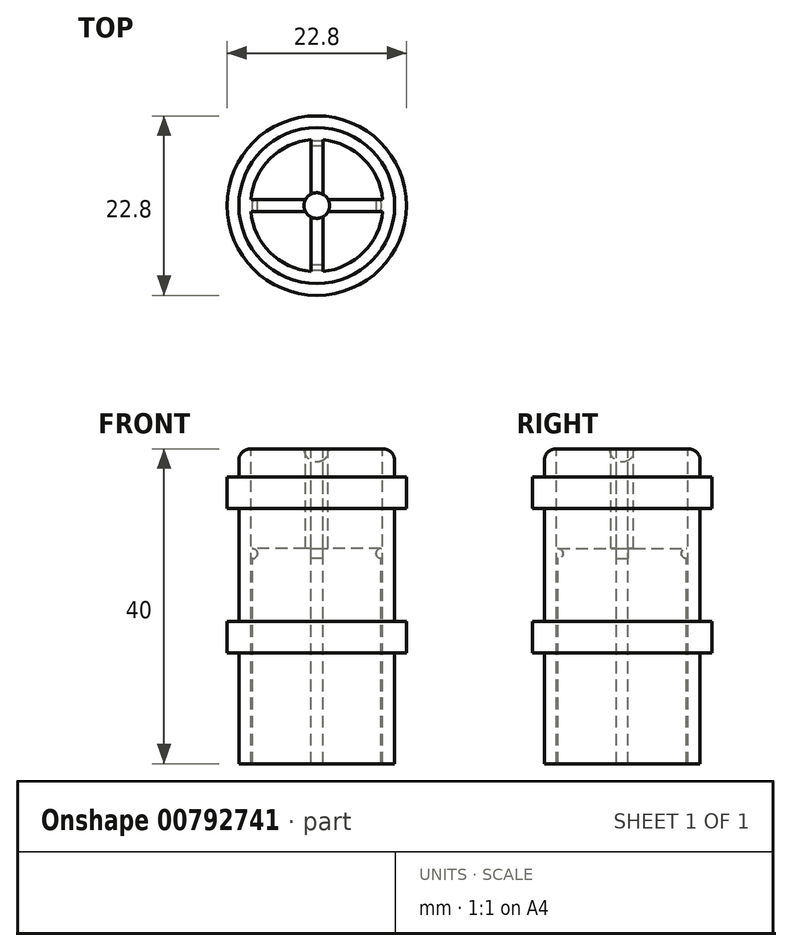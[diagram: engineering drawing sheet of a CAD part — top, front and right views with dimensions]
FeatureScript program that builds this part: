
annotation { "Feature Type Name" : "Feature", "Feature Type Description" : "" }
export const myFeature = defineFeature(function(context is Context, id is Id, definition is map)
    precondition{}
    {
        {
            var Q0;
            Q0=qCreatedBy(makeId("Front.planeOp"),FACE);
            var sketch = newSketch(context, id + "F0", { "sketchPlane" : qUnion([Q0])});
            skLineSegment(sketch, "E0", {"start": v(0, 19.9) * mm, "end": v(8.2, 19.9) * mm});
            skLineSegment(sketch, "E1", {"start": v(8.2, 19.9) * mm, "end": v(8.2, 9.76) * mm});
            skLineSegment(sketch, "E2", {"start": v(8.2, -17.6) * mm, "end": v(0, -17.6) * mm});
            skLineSegment(sketch, "E3", {"start": v(1.62, 22.4) * mm, "end": v(8.4, 22.4) * mm});
            skLineSegment(sketch, "E4", {"start": v(9.9, 20.9) * mm, "end": v(9.9, 18.85) * mm});
            skLineSegment(sketch, "E5", {"start": v(9.9, 18.85) * mm, "end": v(11.4, 18.85) * mm});
            skLineSegment(sketch, "E6", {"start": v(11.4, 18.85) * mm, "end": v(11.4, 14.85) * mm});
            skLineSegment(sketch, "E7", {"start": v(11.4, 14.85) * mm, "end": v(9.9, 14.85) * mm});
            skLineSegment(sketch, "E8", {"start": v(9.9, 14.85) * mm, "end": v(9.9, 0.5) * mm});
            skLineSegment(sketch, "E9", {"start": v(9.9, 0.5) * mm, "end": v(11.4, 0.5) * mm});
            skLineSegment(sketch, "E10", {"start": v(11.4, 0.5) * mm, "end": v(11.4, -3.5) * mm});
            skLineSegment(sketch, "E11", {"start": v(11.4, -3.5) * mm, "end": v(9.9, -3.5) * mm});
            skLineSegment(sketch, "E12", {"start": v(9.9, -3.5) * mm, "end": v(9.9, -17.6) * mm});
            skLineSegment(sketch, "E13", {"start": v(9.9, -17.6) * mm, "end": v(8.2, -17.6) * mm});
            skLineSegment(sketch, "E14", {"start": v(0, 20.78) * mm, "end": v(0, -17.6) * mm});
            skPoint(sketch, "E15.visualSharp", {"position": v(9.9, 22.4) * mm});
            skArc(sketch, "E15.filletArc", {"start": v(9.9, 20.9) * mm, "mid": v(9.46, 21.97) * mm, "end": v(8.4, 22.4) * mm});
            skArc(sketch, "E16", {"start": v(8.2, 9.76) * mm, "mid": v(7.55, 9.1) * mm, "end": v(8.2, 8.46) * mm});
            skLineSegment(sketch, "E17", {"start": v(8.2, 9.76) * mm, "end": v(0, 9.76) * mm});
            skLineSegment(sketch, "E18", {"start": v(8.1, 8.46) * mm, "end": v(8.2, 8.45) * mm});
            skLineSegment(sketch, "E19", {"start": v(8.2, 8.45) * mm, "end": v(0, 8.45) * mm});
            skLineSegment(sketch, "E20", {"start": v(0, 8.45) * mm, "end": v(0, 9.76) * mm});
            skLineSegment(sketch, "E21", {"start": v(8.2, 8.45) * mm, "end": v(8.2, 8.46) * mm});
            skLineSegment(sketch, "E22.trimOffspring", {"start": v(8.2, 8.46) * mm, "end": v(8.2, -17.6) * mm});
            skArc(sketch, "E23", {"start": v(0, 20.78) * mm, "mid": v(1.15, 21.26) * mm, "end": v(1.62, 22.4) * mm});
            skSolve(sketch);
        }
        {
            var Q0;
            {var subQ0=sQuery(id+"F0.wireOp",EDGE,"E0");Q0=makeQuery(id+"F0.imprint","IMPRINT",FACE,{"disambiguationData":[TD([[makeQuery(id+"F0.imprint","IMPRINT",EDGE,{"derivedFrom":subQ0}),1.0]])]});}
            var Q1;
            {var subQ0=sQuery(id+"F0.wireOp",EDGE,"E0");Q1=makeQuery(id+"F0.imprint","IMPRINT",FACE,{"disambiguationData":[TD([[makeQuery(id+"F0.imprint","IMPRINT",EDGE,{"derivedFrom":subQ0}),-1.0]])]});}
            var Q2;
            Q2=sQuery(id+"F0.wireOp",EDGE,"E14");
            revolve(context, id + "F1", {"surfaceOperationType" : NewSurfaceOperationType.NEW, "entities" : qUnion([Q0, Q1]), "axis" : qUnion([Q2]), "revolveType" : RevolveType.FULL});
        }
        {
            var Q0;
            Q0=makeQuery(id+"F1.opRevolve","SWEPT_FACE",FACE,{"disambiguationData":[OSD([sQuery(id+"F0.wireOp",EDGE,"E3")])]});
            var sketch = newSketch(context, id + "F2", { "sketchPlane" : qUnion([Q0])});
            skLineSegment(sketch, "E24", {"start": v(-8.4, 0) * mm, "end": v(8.4, 0) * mm, "construction": true});
            skLineSegment(sketch, "E25", {"start": v(0, 8.4) * mm, "end": v(0, -8.4) * mm, "construction": true});
            skLineSegment(sketch, "E26", {"start": v(0.77, 8.36) * mm, "end": v(0.77, 0.75) * mm});
            skLineSegment(sketch, "E27", {"start": v(0.77, 0.75) * mm, "end": v(8.37, 0.75) * mm});
            skLineSegment(sketch, "E28", {"start": v(8.37, -0.75) * mm, "end": v(0.77, -0.75) * mm});
            skLineSegment(sketch, "E29", {"start": v(0.77, -0.75) * mm, "end": v(0.77, -8.36) * mm});
            skLineSegment(sketch, "E30", {"start": v(-0.73, 8.37) * mm, "end": v(-0.73, 0.75) * mm});
            skLineSegment(sketch, "E31", {"start": v(-0.73, 0.75) * mm, "end": v(-8.37, 0.75) * mm});
            skLineSegment(sketch, "E32", {"start": v(-8.37, -0.75) * mm, "end": v(-0.73, -0.75) * mm});
            skLineSegment(sketch, "E33", {"start": v(-0.73, -0.75) * mm, "end": v(-0.73, -8.37) * mm});
            skSolve(sketch);
        }
        {
            var Q0;
            {var subQ0=sQuery(id+"F2.wireOp",EDGE,"E30");var subQ1=sQuery(id+"F0.wireOp",EDGE,"E3");var subQ2=makeQuery(id+"F1.opRevolve","SWEPT_EDGE",EDGE,{"disambiguationData":[OSD([subQ1,sQuery(id+"F0.wireOp",EDGE,"E15.filletArc")])]});var subQ3=makeQuery(id+"F2.imprint","INTERSECT",VERTEX,{"derivedFrom":[subQ2,subQ0]});Q0=makeQuery(id+"F2.imprint","IMPRINT",FACE,{"disambiguationData":[TD([[makeQuery(id+"F2.imprint","IMPRINT",EDGE,{"disambiguationData":[TD([[subQ3,-1.0]])],"derivedFrom":subQ0}),-1.0]])]});}
            var Q1;
            {var subQ0=sQuery(id+"F2.wireOp",EDGE,"E32");var subQ1=sQuery(id+"F0.wireOp",EDGE,"E3");var subQ2=makeQuery(id+"F1.opRevolve","SWEPT_EDGE",EDGE,{"disambiguationData":[OSD([subQ1,sQuery(id+"F0.wireOp",EDGE,"E15.filletArc")])]});var subQ3=makeQuery(id+"F2.imprint","INTERSECT",VERTEX,{"derivedFrom":[subQ2,subQ0]});Q1=makeQuery(id+"F2.imprint","IMPRINT",FACE,{"disambiguationData":[TD([[makeQuery(id+"F2.imprint","IMPRINT",EDGE,{"disambiguationData":[TD([[subQ3,-1.0]])],"derivedFrom":subQ0}),-1.0]])]});}
            var Q2;
            {var subQ0=sQuery(id+"F2.wireOp",EDGE,"E28");var subQ1=sQuery(id+"F0.wireOp",EDGE,"E3");var subQ2=makeQuery(id+"F1.opRevolve","SWEPT_EDGE",EDGE,{"disambiguationData":[OSD([subQ1,sQuery(id+"F0.wireOp",EDGE,"E15.filletArc")])]});var subQ3=makeQuery(id+"F2.imprint","INTERSECT",VERTEX,{"derivedFrom":[subQ2,subQ0]});Q2=makeQuery(id+"F2.imprint","IMPRINT",FACE,{"disambiguationData":[TD([[makeQuery(id+"F2.imprint","IMPRINT",EDGE,{"disambiguationData":[TD([[subQ3,-1.0]])],"derivedFrom":subQ0}),1.0]])]});}
            var Q3;
            {var subQ0=sQuery(id+"F2.wireOp",EDGE,"E26");var subQ1=sQuery(id+"F0.wireOp",EDGE,"E3");var subQ2=makeQuery(id+"F1.opRevolve","SWEPT_EDGE",EDGE,{"disambiguationData":[OSD([subQ1,sQuery(id+"F0.wireOp",EDGE,"E15.filletArc")])]});var subQ3=makeQuery(id+"F2.imprint","INTERSECT",VERTEX,{"derivedFrom":[subQ2,subQ0]});Q3=makeQuery(id+"F2.imprint","IMPRINT",FACE,{"disambiguationData":[TD([[makeQuery(id+"F2.imprint","IMPRINT",EDGE,{"disambiguationData":[TD([[subQ3,-1.0]])],"derivedFrom":subQ0}),1.0]])]});}
            extrude(context, id + "F3", {"entities" : qUnion([Q0, Q1, Q2, Q3]), "operationType" : NewBodyOperationType.REMOVE, "endBound" : BoundingType.THROUGH_ALL, "oppositeDirection" : true, "depth" : 25 * mm, "offsetDistance" : 25 * mm});
        }
    });
